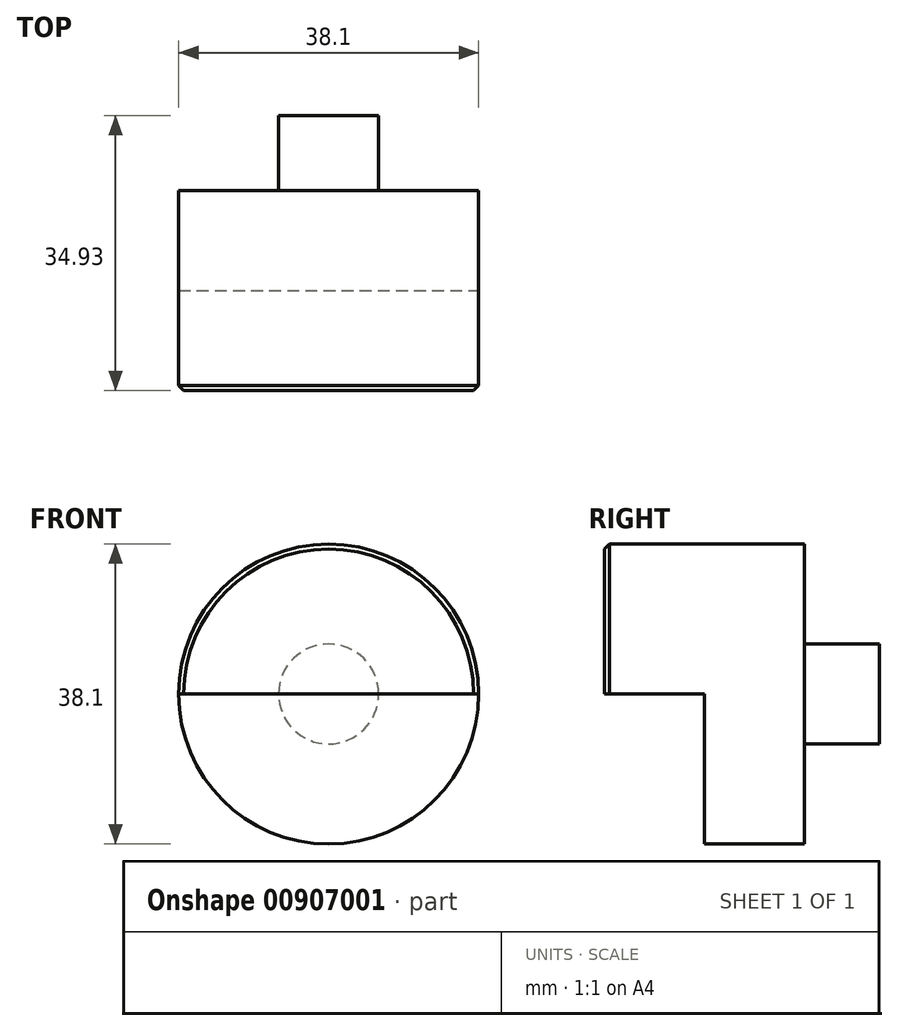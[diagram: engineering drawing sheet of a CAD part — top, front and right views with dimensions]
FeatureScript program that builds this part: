
annotation { "Feature Type Name" : "Feature", "Feature Type Description" : "" }
export const myFeature = defineFeature(function(context is Context, id is Id, definition is map)
    precondition{}
    {
        {
            var Q0;
            Q0=qCreatedBy(makeId("Front.planeOp"),FACE);
            var sketch = newSketch(context, id + "F0", { "sketchPlane" : qUnion([Q0])});
            skCircle(sketch, "E0", {"center": v(0, 0) * mm, "radius": 19.05 * mm});
            skSolve(sketch);
        }
        {
            var Q0;
            Q0=makeQuery(id+"F0.imprint","IMPRINT",FACE,{"disambiguationData":[TD([[makeQuery(id+"F0.imprint","IMPRINT",EDGE,{"derivedFrom":sQuery(id+"F0.wireOp",EDGE,"E0")}),1.0]])]});
            extrude(context, id + "F1", {"entities" : qUnion([Q0]), "depth" : 34.92 * mm, "offsetDistance" : 25.4 * mm});
        }
        {
            var Q0;
            Q0=makeQuery(id+"F1.opExtrude","CAP_FACE",FACE,{"disambiguationData":[OSD([sQuery(id+"F0.wireOp",EDGE,"E0")])],"isStart":true});
            var sketch = newSketch(context, id + "F2", { "sketchPlane" : qUnion([Q0])});
            skCircle(sketch, "E1", {"center": v(0, 0) * mm, "radius": 6.35 * mm});
            skSolve(sketch);
        }
        {
            var Q0;
            Q0=makeQuery(id+"F2.imprint","IMPRINT",FACE,{"disambiguationData":[TD([[makeQuery(id+"F2.imprint","IMPRINT",EDGE,{"derivedFrom":sQuery(id+"F2.wireOp",EDGE,"E1")}),-1.0]])]});
            extrude(context, id + "F3", {"entities" : qUnion([Q0]), "operationType" : NewBodyOperationType.REMOVE, "oppositeDirection" : true, "depth" : 9.52 * mm, "offsetDistance" : 25.4 * mm});
        }
        {
            var Q0;
            Q0=makeQuery(id+"F3.boolean.opBoolean","COPY",EDGE,{"derivedFrom":makeQuery(id+"F3.opExtrude","CAP_EDGE",EDGE,{"disambiguationData":[OSD([sQuery(id+"F2.wireOp",EDGE,"E1")])],"isStart":true})});
            var Q1;
            Q1=makeQuery(id+"F1.opExtrude","CAP_EDGE",EDGE,{"disambiguationData":[OSD([sQuery(id+"F0.wireOp",EDGE,"E0")])],"isStart":false});
            chamfer(context, id + "F4", {"entities" : qUnion([Q0, Q1]), "width" : 0.64 * mm, "tangentPropagation" : true});
        }
        {
            var Q0;
            Q0=makeQuery(id+"F1.opExtrude","CAP_FACE",FACE,{"disambiguationData":[OSD([sQuery(id+"F0.wireOp",EDGE,"E0")])],"isStart":false});
            var sketch = newSketch(context, id + "F5", { "sketchPlane" : qUnion([Q0])});
            skLineSegment(sketch, "E2.bottom", {"start": v(-25.4, -25.4) * mm, "end": v(25.4, -25.4) * mm});
            skLineSegment(sketch, "E2.top", {"start": v(-25.4, 0) * mm, "end": v(25.4, 0) * mm});
            skLineSegment(sketch, "E2.left", {"start": v(-25.4, -25.4) * mm, "end": v(-25.4, 0) * mm});
            skLineSegment(sketch, "E2.right", {"start": v(25.4, -25.4) * mm, "end": v(25.4, 0) * mm});
            skPoint(sketch, "E2.middle", {"position": v(0, -12.7) * mm});
            skSolve(sketch);
        }
        {
            var Q0;
            Q0=makeQuery(id+"F5.imprint","IMPRINT",FACE,{"disambiguationData":[TD([[makeQuery(id+"F5.imprint","IMPRINT",EDGE,{"derivedFrom":sQuery(id+"F5.wireOp",EDGE,"E2.bottom")}),1.0]])]});
            var Q1;
            {var subQ0=sQuery(id+"F5.wireOp",EDGE,"E2.top");var subQ1=sQuery(id+"F0.wireOp",EDGE,"E0");var subQ2=makeQuery(id+"F4.opChamfer","BLEND_EDGE",EDGE,{"blendedFrom":[makeQuery(id+"F1.opExtrude","CAP_EDGE",EDGE,{"disambiguationData":[OSD([subQ1])],"isStart":false}),makeQuery(id+"F1.opExtrude","CAP_FACE",FACE,{"disambiguationData":[OSD([subQ1])],"isStart":false})],"blendedInto":[makeQuery(id+"F1.opExtrude","CAP_FACE",FACE,{"disambiguationData":[OSD([subQ1])],"isStart":false})]});var subQ3=makeQuery(id+"F5.imprint","INTERSECT",VERTEX,{"disambiguationData":[OD(0.0)],"derivedFrom":[subQ2,subQ0]});Q1=makeQuery(id+"F5.imprint","IMPRINT",FACE,{"disambiguationData":[TD([[makeQuery(id+"F5.imprint","IMPRINT",EDGE,{"disambiguationData":[TD([[subQ3,-1.0]])],"derivedFrom":subQ0}),-1.0]])]});}
            extrude(context, id + "F6", {"entities" : qUnion([Q0, Q1]), "operationType" : NewBodyOperationType.REMOVE, "oppositeDirection" : true, "depth" : 12.7 * mm, "offsetDistance" : 25.4 * mm});
        }
    });
